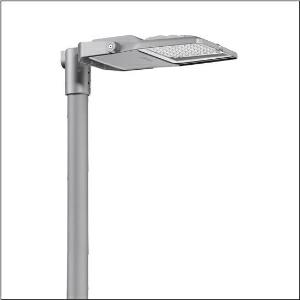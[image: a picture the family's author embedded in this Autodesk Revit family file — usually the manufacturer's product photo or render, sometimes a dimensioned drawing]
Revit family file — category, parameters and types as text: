
# Revit family: floodlight_fl_21_iq_mini___pl64_5xa7771c2e3a_b06c
name_source: partatom
category: Lighting Fixtures
units: mm (PartAtom-declared; Revit-internal decimal feet)

## family parameters
Cut with Voids When Loaded = No
Host = Face
Light Source = No
Part Type = Normal
Room Calculation Point = No
Round Connector Dimension = Use Diameter
Shared = No

## types (1)
- --- (1 x LED, 11790 lm, 87.2 W, 3000K)
    Apparent Load = 87 VA
    CIE Flux Codes = 28 80 98 100 100
    Color Rendering = 70
    Color Temperature = 3000K
    Default Elevation = 1800 mm
    Description = Floodlight FL 21 iQ mini, floodlight, primary light control with lens, of PMMA, primary optical cover: protective disc, of toughened safety glass, transparent, light distribution: PL64, light emission: direct distribution, installation type: surface-mounted, LED, High Power LED, rated luminous flux: 11.790lm, luminous efficacy: 135lm/W, light colour: 730, colour temperature: 3000K, control: Auto-Match, Temp-Guard, Lumen-Switch, Night-Set, Smart-Wire, Light-Fading, Desk-Remote (wireless, voltage-free reading and setting of iQ features in the workshop via application-optimized NFC function/RFID function), optimised constant luminous flux control (CLO 2.0), with terminal, 6-pole, mains connection: 220..240V, AC, 50/60Hz, start of lifetime: 87W, end of service life: 92W, reduction: 40W, luminaire housing, of diecast aluminium, powder-coated, Siteco® metallic grey (DB 702S), corrosivity category C5 mid according to DIN EN ISO 12944, sealing non-destructively replaceable, please order mast flange separately, mast bracket, of steel, galvanised, powder-coated, Siteco® metallic grey (DB 702S), protection rating (complete): IP66, insulation class (complete): insulation class II (safety insulation), certification: CE, ENEC, VDE, protection symbol: D, impact resistance: IK08, permissible operating ambient temperature: -40..+40°C, permissible operating ambient temperature for outdoor applications: -40..+50°C, standard: DIN EN 12944, LABS conformity tested according to VDMA 24364:2018-05, packaging unit: 1 piece

Light Distribution: PL64
    Height = 70 mm
    Lamp = 1 x LED
    Lamp Light Flux = 11790 lm
    Lamp Power = 87.2 W
    Lamp count = 1
    Length = 485 mm
    Luminous efficacy = 135 lm/W
    Manufacturer = Siteco
    ModVariant = No
    Model = 5XA7771C2E3A
    Number of Poles = 1
    OnlyDefault = Yes
    Power Factor = 1
    Product Name = Floodlight FL 21 iQ mini | PL64
    Product group = floodlight | pylon annexe
    ProductGroupID = 6200
    Protection Class = Protection class II
    Protection Degree = IP 66
    RLX_Detail_Level = 1
    RLX_Emergency_Light_Flux = 0 lm
    RLX_Emergency_Type = 0
    RLX_Emergency_Type_DB = No
    RlxData = <blob elided: 101325 chars, md5=f31d9ef4>
    Socket = socket
    Standby Power = 0 W
    System Light Flux = 11790 lm
    System Power = 87 W
    Type Comments = factory setting: luminous flux: 100 % | dim-lin: 254 | 456 mA
    Type Image = l_1007125.jpg
    URL = http://relux.com
    VarID = @adj_098913
    Voltage = 0 V
    Weight = 0.00 kg
    Width = 337 mm

## geometry (parser evidence)
native form markers: Blend x4, Sweep x15
no freeform markers — native parametric forms only
